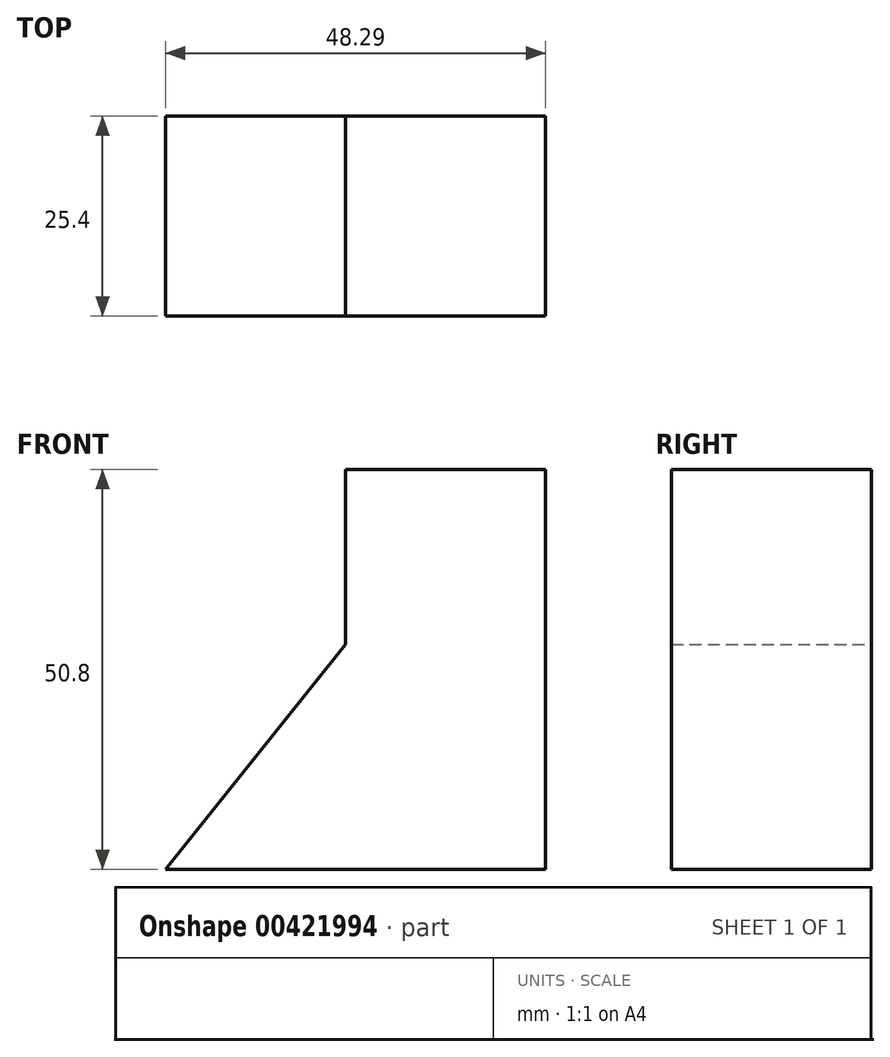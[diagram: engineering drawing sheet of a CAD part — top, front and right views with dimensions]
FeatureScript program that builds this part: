
annotation { "Feature Type Name" : "Feature", "Feature Type Description" : "" }
export const myFeature = defineFeature(function(context is Context, id is Id, definition is map)
    precondition{}
    {
        {
            var Q0;
            Q0=qCreatedBy(makeId("Front.planeOp"),FACE);
            var sketch = newSketch(context, id + "F0", { "sketchPlane" : qUnion([Q0])});
            skLineSegment(sketch, "E0", {"start": v(0, 0) * mm, "end": v(-48.3, 0) * mm});
            skLineSegment(sketch, "E1", {"start": v(0, 0) * mm, "end": v(0, 50.8) * mm});
            skLineSegment(sketch, "E2", {"start": v(0, 50.8) * mm, "end": v(-25.4, 50.8) * mm});
            skLineSegment(sketch, "E3", {"start": v(-25.4, 50.8) * mm, "end": v(-25.4, 28.57) * mm});
            skLineSegment(sketch, "E4", {"start": v(-25.4, 28.57) * mm, "end": v(-48.3, 0) * mm});
            skSolve(sketch);
        }
        {
            var Q0;
            Q0 = qSketchRegion(id + "F0", true);
            extrude(context, id + "F1", {"entities" : qUnion([Q0]), "depth" : 25.4 * mm});
        }
    });
